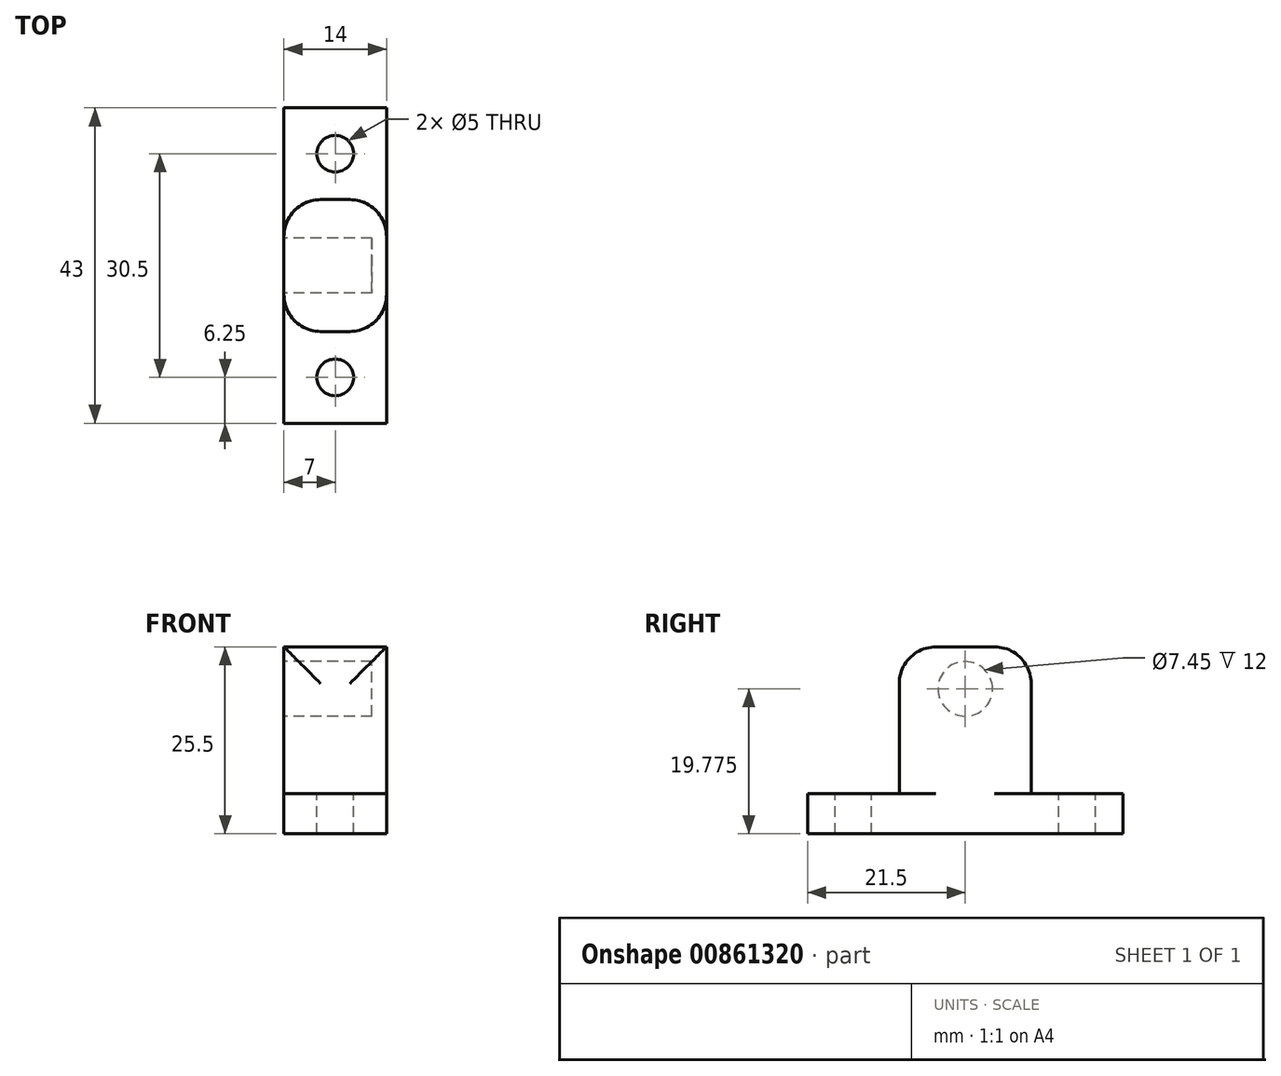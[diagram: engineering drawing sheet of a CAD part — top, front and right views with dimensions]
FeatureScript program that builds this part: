
annotation { "Feature Type Name" : "Feature", "Feature Type Description" : "" }
export const myFeature = defineFeature(function(context is Context, id is Id, definition is map)
    precondition{}
    {
        {
            var Q0;
            Q0=qCreatedBy(makeId("Right.planeOp"),FACE);
            var sketch = newSketch(context, id + "F0", { "sketchPlane" : qUnion([Q0])});
            skLineSegment(sketch, "E0.bottom", {"start": v(0, 0) * mm, "end": v(-43, 0) * mm});
            skLineSegment(sketch, "E0.top", {"start": v(0, 5.5) * mm, "end": v(-43, 5.5) * mm});
            skLineSegment(sketch, "E0.left", {"start": v(0, 0) * mm, "end": v(0, 5.5) * mm});
            skLineSegment(sketch, "E0.right", {"start": v(-43, 0) * mm, "end": v(-43, 5.5) * mm});
            skLineSegment(sketch, "E1.bottom", {"start": v(-30.5, 5.5) * mm, "end": v(-12.5, 5.5) * mm});
            skLineSegment(sketch, "E1.top", {"start": v(-30.5, 25.5) * mm, "end": v(-12.5, 25.5) * mm});
            skLineSegment(sketch, "E1.left", {"start": v(-30.5, 5.5) * mm, "end": v(-30.5, 25.5) * mm});
            skLineSegment(sketch, "E1.right", {"start": v(-12.5, 5.5) * mm, "end": v(-12.5, 25.5) * mm});
            skSolve(sketch);
        }
        {
            var Q0;
            Q0=makeQuery(id+"F0.imprint","IMPRINT",FACE,{"disambiguationData":[TD([[makeQuery(id+"F0.imprint","IMPRINT",EDGE,{"derivedFrom":sQuery(id+"F0.wireOp",EDGE,"E1.top")}),-1.0]])]});
            var Q1;
            Q1=makeQuery(id+"F0.imprint","IMPRINT",FACE,{"disambiguationData":[TD([[makeQuery(id+"F0.imprint","IMPRINT",EDGE,{"derivedFrom":sQuery(id+"F0.wireOp",EDGE,"E0.bottom")}),-1.0]])]});
            extrude(context, id + "F1", {"entities" : qUnion([Q0, Q1]), "depth" : 14 * mm, "offsetDistance" : 25 * mm});
        }
        {
            var Q0;
            {var subQ0=sQuery(id+"F0.wireOp",EDGE,"E0.top");Q0=makeQuery(id+"F1.opExtrude","SWEPT_FACE",FACE,{"disambiguationData":[OSD([subQ0]),TDD([makeQuery(id+"F0.imprint","IMPRINT",EDGE,{"disambiguationData":[TD([[makeQuery(id+"F0.imprint","INTERSECT",VERTEX,{"derivedFrom":[subQ0,sQuery(id+"F0.wireOp",EDGE,"E1.right")]}),1.0]])],"derivedFrom":subQ0})])]});}
            var sketch = newSketch(context, id + "F2", { "sketchPlane" : qUnion([Q0])});
            skCircle(sketch, "E2", {"center": v(7, -6.25) * mm, "radius": 2.5 * mm});
            skCircle(sketch, "E3", {"center": v(7, -36.75) * mm, "radius": 2.5 * mm});
            skSolve(sketch);
        }
        {
            var Q0;
            Q0=makeQuery(id+"F2.imprint","IMPRINT",FACE,{"disambiguationData":[TD([[makeQuery(id+"F2.imprint","IMPRINT",EDGE,{"derivedFrom":sQuery(id+"F2.wireOp",EDGE,"E2")}),1.0]])]});
            var Q1;
            Q1=makeQuery(id+"F2.imprint","IMPRINT",FACE,{"disambiguationData":[TD([[makeQuery(id+"F2.imprint","IMPRINT",EDGE,{"derivedFrom":sQuery(id+"F2.wireOp",EDGE,"E3")}),1.0]])]});
            extrude(context, id + "F3", {"entities" : qUnion([Q0, Q1]), "operationType" : NewBodyOperationType.REMOVE, "oppositeDirection" : true, "depth" : 5.8 * mm, "offsetDistance" : 25 * mm});
        }
        {
            var Q0;
            Q0=makeQuery(id+"F1.opExtrude","SWEPT_EDGE",EDGE,{"disambiguationData":[OSD([sQuery(id+"F0.wireOp",EDGE,"E1.top"),sQuery(id+"F0.wireOp",EDGE,"E1.left")])]});
            var Q1;
            Q1=makeQuery(id+"F1.opExtrude","SWEPT_EDGE",EDGE,{"disambiguationData":[OSD([sQuery(id+"F0.wireOp",EDGE,"E1.top"),sQuery(id+"F0.wireOp",EDGE,"E1.right")])]});
            var Q2;
            Q2=makeQuery(id+"F1.opExtrude","CAP_EDGE",EDGE,{"disambiguationData":[OSD([sQuery(id+"F0.wireOp",EDGE,"E1.left")])],"isStart":false});
            var Q3;
            Q3=makeQuery(id+"F1.opExtrude","CAP_EDGE",EDGE,{"disambiguationData":[OSD([sQuery(id+"F0.wireOp",EDGE,"E1.right")])],"isStart":false});
            var Q4;
            Q4=makeQuery(id+"F1.opExtrude","CAP_EDGE",EDGE,{"disambiguationData":[OSD([sQuery(id+"F0.wireOp",EDGE,"E1.right")])],"isStart":true});
            var Q5;
            Q5=makeQuery(id+"F1.opExtrude","CAP_EDGE",EDGE,{"disambiguationData":[OSD([sQuery(id+"F0.wireOp",EDGE,"E1.left")])],"isStart":true});
            fillet(context, id + "F4", {"entities" : qUnion([Q0, Q1, Q2, Q3, Q4, Q5]), "radius" : 5 * mm, "tangentPropagation" : true, "allowEdgeOverflow" : false});
        }
        {
            var Q0;
            Q0=makeQuery(id+"F0.imprint","IMPRINT",FACE,{"disambiguationData":[TD([[makeQuery(id+"F0.imprint","IMPRINT",EDGE,{"derivedFrom":sQuery(id+"F0.wireOp",EDGE,"E1.top")}),-1.0]])]});
            var sketch = newSketch(context, id + "F5", { "sketchPlane" : qUnion([Q0])});
            skCircle(sketch, "E4", {"center": v(-21.5, 19.78) * mm, "radius": 3.73 * mm});
            skSolve(sketch);
        }
        {
            var Q0;
            Q0=makeQuery(id+"F5.imprint","IMPRINT",FACE,{"disambiguationData":[TD([[makeQuery(id+"F5.imprint","IMPRINT",EDGE,{"derivedFrom":sQuery(id+"F5.wireOp",EDGE,"E4")}),1.0]])]});
            var Q1;
            Q1=sQuery(id+"F5.wireOp",EDGE,"E4");
            extrude(context, id + "F6", {"entities" : qUnion([Q0]), "operationType" : NewBodyOperationType.REMOVE, "surfaceEntities" : qUnion([Q1]), "depth" : 12 * mm, "offsetDistance" : 25 * mm});
        }
    });
